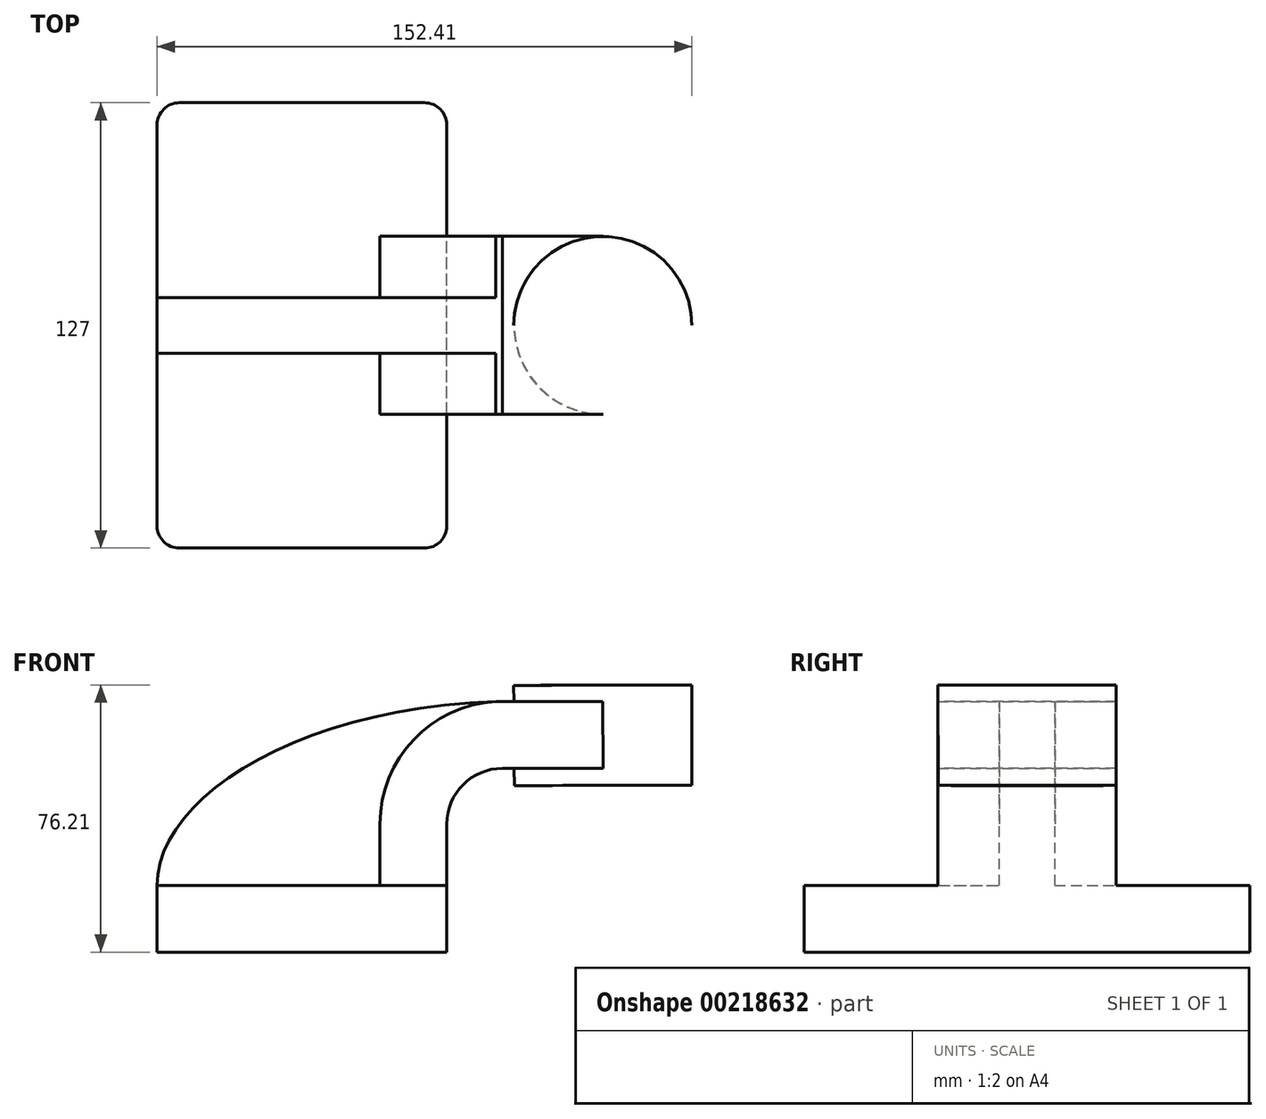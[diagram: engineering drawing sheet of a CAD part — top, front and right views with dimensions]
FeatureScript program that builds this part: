
annotation { "Feature Type Name" : "Feature", "Feature Type Description" : "" }
export const myFeature = defineFeature(function(context is Context, id is Id, definition is map)
    precondition{}
    {
        {
            var Q0;
            Q0=qCreatedBy(makeId("Front.planeOp"),FACE);
            var sketch = newSketch(context, id + "F0", { "sketchPlane" : qUnion([Q0])});
            skLineSegment(sketch, "E0.bottom", {"start": v(-41.28, -9.53) * mm, "end": v(41.28, -9.53) * mm});
            skLineSegment(sketch, "E0.top", {"start": v(-41.28, 9.53) * mm, "end": v(41.28, 9.53) * mm});
            skLineSegment(sketch, "E0.left", {"start": v(-41.28, -9.53) * mm, "end": v(-41.28, 9.53) * mm});
            skLineSegment(sketch, "E0.right", {"start": v(41.28, -9.53) * mm, "end": v(41.28, 9.53) * mm});
            skPoint(sketch, "E0.middle", {"position": v(0, 0) * mm});
            skLineSegment(sketch, "E1.bottom", {"start": v(111.12, 38.1) * mm, "end": v(60.32, 38.1) * mm});
            skLineSegment(sketch, "E1.top", {"start": v(111.12, 66.68) * mm, "end": v(60.32, 66.68) * mm});
            skLineSegment(sketch, "E1.left", {"start": v(111.12, 38.1) * mm, "end": v(111.12, 66.68) * mm});
            skLineSegment(sketch, "E1.right", {"start": v(60.32, 38.1) * mm, "end": v(60.32, 66.68) * mm});
            skPoint(sketch, "E1.middle", {"position": v(85.72, 52.39) * mm});
            skLineSegment(sketch, "E2", {"start": v(41.27, 9.53) * mm, "end": v(41.27, 27) * mm});
            skArc(sketch, "E3", {"start": v(41.27, 27) * mm, "mid": v(45.92, 38.23) * mm, "end": v(57.15, 42.88) * mm});
            skLineSegment(sketch, "E4", {"start": v(57.15, 42.88) * mm, "end": v(85.82, 42.88) * mm});
            skFitSpline(sketch, "E5", {"points": [v(-41.28, 9.53) * mm, v(57.15, 61.93) * mm], "startDerivative": vector(-0.31, 73.78) * mm, "endDerivative": vector(176.05, 3.93) * mm});
            skLineSegment(sketch, "E6.0", {"start": v(57.15, 61.93) * mm, "end": v(85.82, 61.93) * mm});
            skArc(sketch, "E6.1", {"start": v(22.23, 27) * mm, "mid": v(32.45, 51.7) * mm, "end": v(57.15, 61.93) * mm});
            skLineSegment(sketch, "E6.2", {"start": v(22.23, 9.53) * mm, "end": v(22.23, 27) * mm});
            skLineSegment(sketch, "E7", {"start": v(85.72, 66.68) * mm, "end": v(85.82, 38.1) * mm});
            skSolve(sketch);
        }
        {
            var Q0;
            Q0=makeQuery(id+"F0.imprint","IMPRINT",FACE,{"disambiguationData":[TD([[makeQuery(id+"F0.imprint","IMPRINT",EDGE,{"derivedFrom":sQuery(id+"F0.wireOp",EDGE,"E0.bottom")}),1.0]])]});
            extrude(context, id + "F1", {"entities" : qUnion([Q0]), "endBound" : BoundingType.SYMMETRIC, "depth" : 127 * mm});
        }
        {
            var Q0;
            {var subQ6=sQuery(id+"F0.wireOp",EDGE,"E2");Q0=makeQuery(id+"F0.imprint","IMPRINT",FACE,{"disambiguationData":[TD([[makeQuery(id+"F0.imprint","IMPRINT",EDGE,{"derivedFrom":subQ6}),1.0]])]});}
            var Q1;
            {var subQ0=sQuery(id+"F0.wireOp",EDGE,"E4");var subQ1=sQuery(id+"F0.wireOp",EDGE,"E1.right");var subQ2=makeQuery(id+"F0.imprint","INTERSECT",VERTEX,{"derivedFrom":[subQ1,subQ0]});Q1=makeQuery(id+"F0.imprint","IMPRINT",FACE,{"disambiguationData":[TD([[makeQuery(id+"F0.imprint","IMPRINT",EDGE,{"disambiguationData":[TD([[subQ2,-1.0]])],"derivedFrom":subQ1}),-1.0]])]});}
            extrude(context, id + "F2", {"entities" : qUnion([Q0, Q1]), "operationType" : NewBodyOperationType.ADD, "endBound" : BoundingType.SYMMETRIC, "depth" : 50.8 * mm});
        }
        {
            var Q0;
            {var subQ3=sQuery(id+"F0.wireOp",EDGE,"E6.2");Q0=makeQuery(id+"F0.imprint","IMPRINT",FACE,{"disambiguationData":[TD([[makeQuery(id+"F0.imprint","IMPRINT",EDGE,{"derivedFrom":subQ3}),1.0]])]});}
            extrude(context, id + "F3", {"entities" : qUnion([Q0]), "operationType" : NewBodyOperationType.ADD, "endBound" : BoundingType.SYMMETRIC, "depth" : 15.88 * mm});
        }
        {
            var Q0;
            {var subQ4=sQuery(id+"F0.wireOp",EDGE,"E1.left");Q0=makeQuery(id+"F0.imprint","IMPRINT",FACE,{"disambiguationData":[TD([[makeQuery(id+"F0.imprint","IMPRINT",EDGE,{"derivedFrom":subQ4}),1.0]])]});}
            var Q1;
            Q1=sQuery(id+"F0.wireOp",EDGE,"E7");
            revolve(context, id + "F4", {"operationType" : NewBodyOperationType.ADD, "entities" : qUnion([Q0]), "axis" : qUnion([Q1]), "revolveType" : RevolveType.FULL});
        }
        {
            var Q0;
            Q0=makeQuery(id+"F1.opExtrude","CAP_EDGE",EDGE,{"disambiguationData":[OSD([sQuery(id+"F0.wireOp",EDGE,"E0.left")])],"isStart":false});
            var Q1;
            Q1=makeQuery(id+"F1.opExtrude","CAP_EDGE",EDGE,{"disambiguationData":[OSD([sQuery(id+"F0.wireOp",EDGE,"E0.right")])],"isStart":false});
            var Q2;
            Q2=makeQuery(id+"F1.opExtrude","CAP_EDGE",EDGE,{"disambiguationData":[OSD([sQuery(id+"F0.wireOp",EDGE,"E0.right")])],"isStart":true});
            var Q3;
            Q3=makeQuery(id+"F1.opExtrude","CAP_EDGE",EDGE,{"disambiguationData":[OSD([sQuery(id+"F0.wireOp",EDGE,"E0.left")])],"isStart":true});
            fillet(context, id + "F5", {"entities" : qUnion([Q0, Q1, Q2, Q3]), "radius" : 6.35 * mm, "tangentPropagation" : true, "allowEdgeOverflow" : false});
        }
    });
